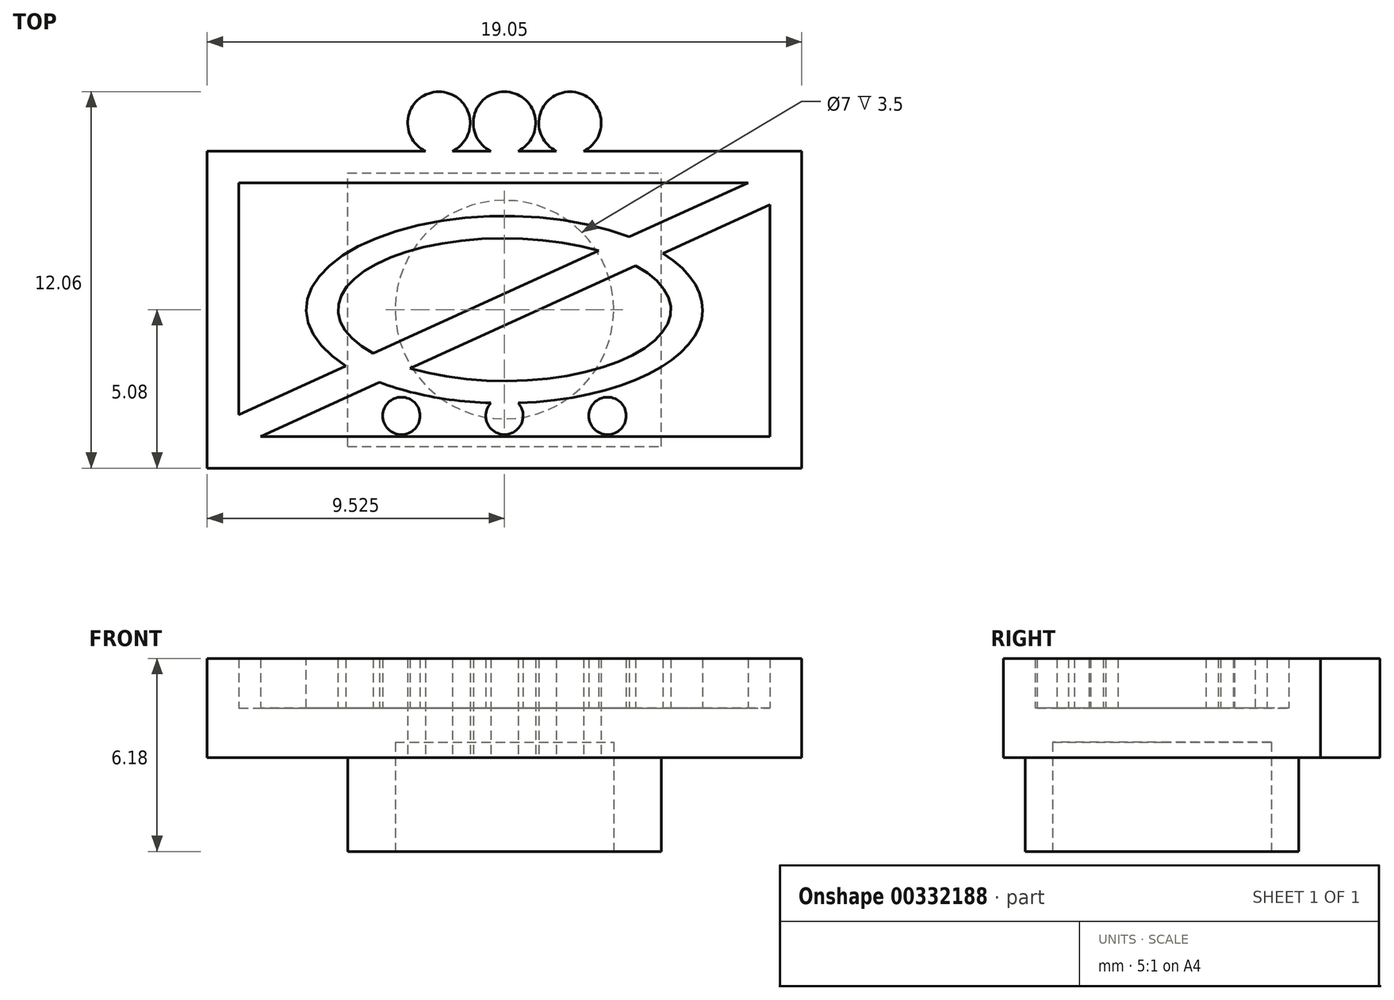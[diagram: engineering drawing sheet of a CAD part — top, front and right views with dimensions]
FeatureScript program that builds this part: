
annotation { "Feature Type Name" : "Feature", "Feature Type Description" : "" }
export const myFeature = defineFeature(function(context is Context, id is Id, definition is map)
    precondition{}
    {
        {
            var Q0;
            Q0=qCreatedBy(makeId("Top.planeOp"),FACE);
            var sketch = newSketch(context, id + "F0", { "sketchPlane" : qUnion([Q0])});
            skLineSegment(sketch, "E0.bottom", {"start": v(-19.05, 10.16) * mm, "end": v(0, 10.16) * mm});
            skLineSegment(sketch, "E0.top", {"start": v(-19.05, 0) * mm, "end": v(0, 0) * mm});
            skLineSegment(sketch, "E0.left", {"start": v(-19.05, 10.16) * mm, "end": v(-19.05, 0) * mm});
            skLineSegment(sketch, "E0.right", {"start": v(0, 10.16) * mm, "end": v(0, 0) * mm});
            skCircle(sketch, "E1", {"center": v(-9.53, 11.06) * mm, "radius": 1 * mm});
            skLineSegment(sketch, "E2", {"start": v(-9.52, 10.16) * mm, "end": v(-9.52, 0) * mm, "construction": true});
            skCircle(sketch, "E3", {"center": v(-11.62, 11.06) * mm, "radius": 1 * mm});
            skCircle(sketch, "E4.MirrorC", {"center": v(-7.43, 11.06) * mm, "radius": 1 * mm});
            skSolve(sketch);
        }
        {
            var Q0;
            Q0=qSketchRegion(id+"F0",true);
            extrude(context, id + "F1", {"entities" : qUnion([Q0]), "depth" : 3.17 * mm});
        }
        {
            var Q0;
            Q0=makeQuery(id+"F1.opExtrude","CAP_FACE",FACE,{"disambiguationData":[OSD([sQuery(id+"F0.wireOp",EDGE,"E0.bottom"),sQuery(id+"F0.wireOp",EDGE,"E0.top"),sQuery(id+"F0.wireOp",EDGE,"E0.left"),sQuery(id+"F0.wireOp",EDGE,"E0.right")])],"isStart":false});
            var sketch = newSketch(context, id + "F2", { "sketchPlane" : qUnion([Q0])});
            skLineSegment(sketch, "E5.bottom", {"start": v(-18.03, 9.14) * mm, "end": v(-1.02, 9.14) * mm});
            skLineSegment(sketch, "E5.top", {"start": v(-18.03, 1.02) * mm, "end": v(-1.02, 1.02) * mm});
            skLineSegment(sketch, "E5.left", {"start": v(-18.03, 9.14) * mm, "end": v(-18.03, 1.02) * mm});
            skLineSegment(sketch, "E5.right", {"start": v(-1.02, 9.14) * mm, "end": v(-1.02, 1.02) * mm});
            skSolve(sketch);
        }
        {
            var Q0;
            Q0=qSketchRegion(id+"F2",true);
            extrude(context, id + "F3", {"entities" : qUnion([Q0]), "operationType" : NewBodyOperationType.REMOVE, "oppositeDirection" : true, "depth" : 1.59 * mm});
        }
        {
            var Q0;
            Q0=makeQuery(id+"F3.boolean.opBoolean","COPY",FACE,{"derivedFrom":makeQuery(id+"F3.opExtrude","CAP_FACE",FACE,{"disambiguationData":[OSD([sQuery(id+"F2.wireOp",EDGE,"E5.bottom"),sQuery(id+"F2.wireOp",EDGE,"E5.top"),sQuery(id+"F2.wireOp",EDGE,"E5.left"),sQuery(id+"F2.wireOp",EDGE,"E5.right")])],"isStart":false})});
            var sketch = newSketch(context, id + "F4", { "sketchPlane" : qUnion([Q0])});
            skLineSegment(sketch, "E6", {"start": v(-9.53, 5.59) * mm, "end": v(-1.72, 9.14) * mm});
            skLineSegment(sketch, "E7", {"start": v(-1.72, 9.14) * mm, "end": v(-1.02, 9.14) * mm});
            skLineSegment(sketch, "E8", {"start": v(-1.02, 9.14) * mm, "end": v(-1.02, 8.44) * mm});
            skLineSegment(sketch, "E9", {"start": v(-1.02, 8.44) * mm, "end": v(-8.4, 5.08) * mm});
            skLineSegment(sketch, "E10", {"start": v(-9.52, 4.57) * mm, "end": v(-17.33, 1.02) * mm});
            skLineSegment(sketch, "E11", {"start": v(-17.33, 1.02) * mm, "end": v(-18.03, 1.02) * mm});
            skLineSegment(sketch, "E12", {"start": v(-18.03, 1.02) * mm, "end": v(-18.03, 1.72) * mm});
            skLineSegment(sketch, "E13", {"start": v(-18.03, 1.72) * mm, "end": v(-10.64, 5.08) * mm});
            skLineSegment(sketch, "E14", {"start": v(-9.52, 9.14) * mm, "end": v(-9.52, 1.02) * mm, "construction": true});
            skLineSegment(sketch, "E15", {"start": v(-18.03, 5.08) * mm, "end": v(-1.02, 5.08) * mm, "construction": true});
            skPoint(sketch, "E16", {"position": v(-9.52, 5.08) * mm});
            skLineSegment(sketch, "E17", {"start": v(-9.52, 5.59) * mm, "end": v(-10.64, 5.08) * mm});
            skLineSegment(sketch, "E18", {"start": v(-9.52, 4.57) * mm, "end": v(-8.4, 5.08) * mm});
            skSolve(sketch);
        }
        {
            var Q0;
            Q0=qSketchRegion(id+"F4",true);
            var Q1;
            Q1=makeQuery(id+"F1.opExtrude","CAP_FACE",FACE,{"disambiguationData":[OSD([sQuery(id+"F0.wireOp",EDGE,"E0.bottom"),sQuery(id+"F0.wireOp",EDGE,"E0.top"),sQuery(id+"F0.wireOp",EDGE,"E0.left"),sQuery(id+"F0.wireOp",EDGE,"E0.right"),sQuery(id+"F0.wireOp",EDGE,"XctMcTzM-jzK6-gSmv-2nxO-Hmrl2WoydrkH.bottom"),sQuery(id+"F0.wireOp",EDGE,"XctMcTzM-jzK6-gSmv-2nxO-Hmrl2WoydrkH.left"),sQuery(id+"F0.wireOp",EDGE,"XctMcTzM-jzK6-gSmv-2nxO-Hmrl2WoydrkH.right")])],"isStart":false});
            extrude(context, id + "F5", {"entities" : qUnion([Q0]), "operationType" : NewBodyOperationType.ADD, "endBound" : BoundingType.UP_TO_SURFACE, "endBoundEntityFace" : qUnion([Q1]), "depth" : 25.4 * mm});
        }
        {
            var Q0;
            {var subQ0=sQuery(id+"F2.wireOp",EDGE,"E5.bottom");var subQ1=sQuery(id+"F2.wireOp",EDGE,"E5.left");Q0=makeQuery(id+"F5.boolean.opBoolean","SPLIT",FACE,{"disambiguationData":[TD([makeQuery(id+"F3.boolean.opBoolean","COPY",FACE,{"derivedFrom":makeQuery(id+"F3.opExtrude","SWEPT_FACE",FACE,{"disambiguationData":[OSD([subQ0])]})})])],"derivedFrom":makeQuery(id+"F3.boolean.opBoolean","COPY",FACE,{"derivedFrom":makeQuery(id+"F3.opExtrude","CAP_FACE",FACE,{"disambiguationData":[OSD([subQ0,sQuery(id+"F2.wireOp",EDGE,"E5.top"),subQ1,sQuery(id+"F2.wireOp",EDGE,"E5.right")])],"isStart":false})})});}
            var sketch = newSketch(context, id + "F6", { "sketchPlane" : qUnion([Q0])});
            skLineSegment(sketch, "E19", {"start": v(-9.52, 10.16) * mm, "end": v(-9.52, 0) * mm, "construction": true});
            skLineSegment(sketch, "E20", {"start": v(-19.05, 5.08) * mm, "end": v(0, 5.08) * mm, "construction": true});
            skEllipse(sketch, "E21", {"center": v(-9.52, 5.08) * mm, "majorRadius": 5.33 * mm, "minorRadius": 2.29 * mm, "majorAxis": v(-1, 0)});
            skEllipse(sketch, "E22", {"center": v(-9.52, 5.08) * mm, "majorRadius": 6.35 * mm, "minorRadius": 3 * mm, "majorAxis": v(1, 0)});
            skSolve(sketch);
        }
        {
            var Q0;
            Q0=qSketchRegion(id+"F6",true);
            var Q1;
            Q1=makeQuery(id+"F5.boolean.opBoolean","MERGE",FACE,{"derivedFrom":[makeQuery(id+"F1.opExtrude","CAP_FACE",FACE,{"disambiguationData":[OSD([sQuery(id+"F0.wireOp",EDGE,"E0.bottom"),sQuery(id+"F0.wireOp",EDGE,"E0.top"),sQuery(id+"F0.wireOp",EDGE,"E0.left"),sQuery(id+"F0.wireOp",EDGE,"E0.right"),sQuery(id+"F0.wireOp",EDGE,"XctMcTzM-jzK6-gSmv-2nxO-Hmrl2WoydrkH.bottom"),sQuery(id+"F0.wireOp",EDGE,"XctMcTzM-jzK6-gSmv-2nxO-Hmrl2WoydrkH.left"),sQuery(id+"F0.wireOp",EDGE,"XctMcTzM-jzK6-gSmv-2nxO-Hmrl2WoydrkH.right")])],"isStart":false}),makeQuery(id+"F5.opExtrude","CAP_FACE",FACE,{"disambiguationData":[OSD([sQuery(id+"F4.wireOp",EDGE,"E6"),sQuery(id+"F4.wireOp",EDGE,"E7"),sQuery(id+"F4.wireOp",EDGE,"E8"),sQuery(id+"F4.wireOp",EDGE,"E9"),sQuery(id+"F4.wireOp",EDGE,"E10"),sQuery(id+"F4.wireOp",EDGE,"E11"),sQuery(id+"F4.wireOp",EDGE,"E12"),sQuery(id+"F4.wireOp",EDGE,"E13"),sQuery(id+"F4.wireOp",EDGE,"E17"),sQuery(id+"F4.wireOp",EDGE,"E18"),sQuery(id+"F4.wireOp",EDGE,"2eZ3HgfS-F6HE-pDFD-BtrP-3SBC7ZAuQREh"),sQuery(id+"F4.wireOp",EDGE,"egwDE0gL-gJxL-a5VO-DP01-p7e11LL6TNIh"),sQuery(id+"F4.wireOp",EDGE,"Oc6yrfE5-Wmlw-YOVM-BoAX-kQYr9RLupFyV"),sQuery(id+"F4.wireOp",EDGE,"HKjVjBGv-TE9a-NIGQ-HE8n-yFD3IG2zp62e")])],"isStart":false})]});
            extrude(context, id + "F7", {"entities" : qUnion([Q0]), "operationType" : NewBodyOperationType.ADD, "endBound" : BoundingType.UP_TO_SURFACE, "endBoundEntityFace" : qUnion([Q1]), "depth" : 25.4 * mm});
        }
        {
            var Q0;
            {var subQ1=sQuery(id+"F2.wireOp",EDGE,"E5.top");var subQ4=makeQuery(id+"F3.boolean.opBoolean","COPY",FACE,{"derivedFrom":makeQuery(id+"F3.opExtrude","SWEPT_FACE",FACE,{"disambiguationData":[OSD([subQ1])]})});var subQ6=sQuery(id+"F2.wireOp",EDGE,"E5.right");Q0=makeQuery(id+"F7.boolean.opBoolean","SPLIT",FACE,{"disambiguationData":[TD([subQ4])],"derivedFrom":makeQuery(id+"F5.boolean.opBoolean","SPLIT",FACE,{"disambiguationData":[TD([subQ4])],"derivedFrom":makeQuery(id+"F3.boolean.opBoolean","COPY",FACE,{"derivedFrom":makeQuery(id+"F3.opExtrude","CAP_FACE",FACE,{"disambiguationData":[OSD([sQuery(id+"F2.wireOp",EDGE,"E5.bottom"),subQ1,sQuery(id+"F2.wireOp",EDGE,"E5.left"),subQ6])],"isStart":false})})})});}
            var sketch = newSketch(context, id + "F8", { "sketchPlane" : qUnion([Q0])});
            skLineSegment(sketch, "E23", {"start": v(-19.05, 1.68) * mm, "end": v(-1.02, 1.68) * mm, "construction": true});
            skCircle(sketch, "E24", {"center": v(-12.83, 1.68) * mm, "radius": 0.6 * mm});
            skLineSegment(sketch, "E25", {"start": v(-9.53, 10.16) * mm, "end": v(-9.53, 0) * mm, "construction": true});
            skCircle(sketch, "E26.MirrorC", {"center": v(-6.22, 1.68) * mm, "radius": 0.6 * mm});
            skCircle(sketch, "E27", {"center": v(-9.53, 1.68) * mm, "radius": 0.6 * mm});
            skSolve(sketch);
        }
        {
            var Q0;
            Q0 = qSketchRegion(id + "F8", true);
            var Q1;
            Q1=makeQuery(id+"F7.boolean.opBoolean","MERGE",FACE,{"derivedFrom":[makeQuery(id+"F5.boolean.opBoolean","MERGE",FACE,{"derivedFrom":[makeQuery(id+"F1.opExtrude","CAP_FACE",FACE,{"disambiguationData":[OSD([sQuery(id+"F0.wireOp",EDGE,"E0.bottom"),sQuery(id+"F0.wireOp",EDGE,"E0.top"),sQuery(id+"F0.wireOp",EDGE,"E0.left"),sQuery(id+"F0.wireOp",EDGE,"E0.right"),sQuery(id+"F0.wireOp",EDGE,"XctMcTzM-jzK6-gSmv-2nxO-Hmrl2WoydrkH.bottom"),sQuery(id+"F0.wireOp",EDGE,"XctMcTzM-jzK6-gSmv-2nxO-Hmrl2WoydrkH.left"),sQuery(id+"F0.wireOp",EDGE,"XctMcTzM-jzK6-gSmv-2nxO-Hmrl2WoydrkH.right")])],"isStart":false}),makeQuery(id+"F5.opExtrude","CAP_FACE",FACE,{"disambiguationData":[OSD([sQuery(id+"F4.wireOp",EDGE,"E6"),sQuery(id+"F4.wireOp",EDGE,"E7"),sQuery(id+"F4.wireOp",EDGE,"E8"),sQuery(id+"F4.wireOp",EDGE,"E9"),sQuery(id+"F4.wireOp",EDGE,"E10"),sQuery(id+"F4.wireOp",EDGE,"E11"),sQuery(id+"F4.wireOp",EDGE,"E12"),sQuery(id+"F4.wireOp",EDGE,"E13"),sQuery(id+"F4.wireOp",EDGE,"E17"),sQuery(id+"F4.wireOp",EDGE,"E18"),sQuery(id+"F4.wireOp",EDGE,"2eZ3HgfS-F6HE-pDFD-BtrP-3SBC7ZAuQREh"),sQuery(id+"F4.wireOp",EDGE,"egwDE0gL-gJxL-a5VO-DP01-p7e11LL6TNIh"),sQuery(id+"F4.wireOp",EDGE,"Oc6yrfE5-Wmlw-YOVM-BoAX-kQYr9RLupFyV"),sQuery(id+"F4.wireOp",EDGE,"HKjVjBGv-TE9a-NIGQ-HE8n-yFD3IG2zp62e")])],"isStart":false})]}),makeQuery(id+"F7.opExtrude","CAP_FACE",FACE,{"disambiguationData":[OSD([sQuery(id+"F6.wireOp",EDGE,"E21"),sQuery(id+"F6.wireOp",EDGE,"E22")])],"isStart":false})]});
            extrude(context, id + "F9", {"entities" : qUnion([Q0]), "operationType" : NewBodyOperationType.ADD, "endBound" : BoundingType.UP_TO_SURFACE, "endBoundEntityFace" : qUnion([Q1]), "depth" : 25.4 * mm});
        }
        {
            var Q0;
            Q0=makeQuery(id+"F1.opExtrude","CAP_FACE",FACE,{"disambiguationData":[OSD([sQuery(id+"F0.wireOp",EDGE,"E0.bottom"),sQuery(id+"F0.wireOp",EDGE,"E0.top"),sQuery(id+"F0.wireOp",EDGE,"E0.left"),sQuery(id+"F0.wireOp",EDGE,"E0.right"),sQuery(id+"F0.wireOp",EDGE,"E1"),sQuery(id+"F0.wireOp",EDGE,"E3"),sQuery(id+"F0.wireOp",EDGE,"E4.MirrorC")])],"isStart":true});
            var sketch = newSketch(context, id + "F10", { "sketchPlane" : qUnion([Q0])});
            skLineSegment(sketch, "E28.bottom", {"start": v(-14.55, -0.7) * mm, "end": v(-4.5, -0.7) * mm});
            skLineSegment(sketch, "E28.top", {"start": v(-14.55, -9.46) * mm, "end": v(-4.5, -9.46) * mm});
            skLineSegment(sketch, "E28.left", {"start": v(-14.55, -0.7) * mm, "end": v(-14.55, -9.46) * mm});
            skLineSegment(sketch, "E28.right", {"start": v(-4.5, -0.7) * mm, "end": v(-4.5, -9.46) * mm});
            skSolve(sketch);
        }
        {
            var Q0;
            Q0 = qSketchRegion(id + "F10", true);
            extrude(context, id + "F11", {"entities" : qUnion([Q0]), "operationType" : NewBodyOperationType.ADD, "depth" : 3 * mm, "offsetDistance" : 25 * mm});
        }
        {
            var Q0;
            Q0=makeQuery(id+"F11.opExtrude","CAP_FACE",FACE,{"disambiguationData":[OSD([sQuery(id+"F10.wireOp",EDGE,"E28.bottom"),sQuery(id+"F10.wireOp",EDGE,"E28.top"),sQuery(id+"F10.wireOp",EDGE,"E28.left"),sQuery(id+"F10.wireOp",EDGE,"E28.right")])],"isStart":false});
            var sketch = newSketch(context, id + "F12", { "sketchPlane" : qUnion([Q0])});
            skCircle(sketch, "E29", {"center": v(-9.52, -5.08) * mm, "radius": 3.5 * mm});
            skLineSegment(sketch, "E30", {"start": v(-19.05, -5.08) * mm, "end": v(0, -5.08) * mm, "construction": true});
            skPoint(sketch, "E30.endSnap0", {"position": v(-4.5, -5.08) * mm});
            skLineSegment(sketch, "E31", {"start": v(-9.53, 0) * mm, "end": v(-9.53, -9.46) * mm, "construction": true});
            skSolve(sketch);
        }
        {
            var Q0;
            Q0=makeQuery(id+"F12.imprint","IMPRINT",FACE,{"disambiguationData":[TD([[makeQuery(id+"F12.imprint","IMPRINT",EDGE,{"derivedFrom":sQuery(id+"F12.wireOp",EDGE,"E29")}),1.0]])]});
            extrude(context, id + "F13", {"entities" : qUnion([Q0]), "operationType" : NewBodyOperationType.REMOVE, "oppositeDirection" : true, "depth" : 3.5 * mm, "offsetDistance" : 25 * mm});
        }
    });
